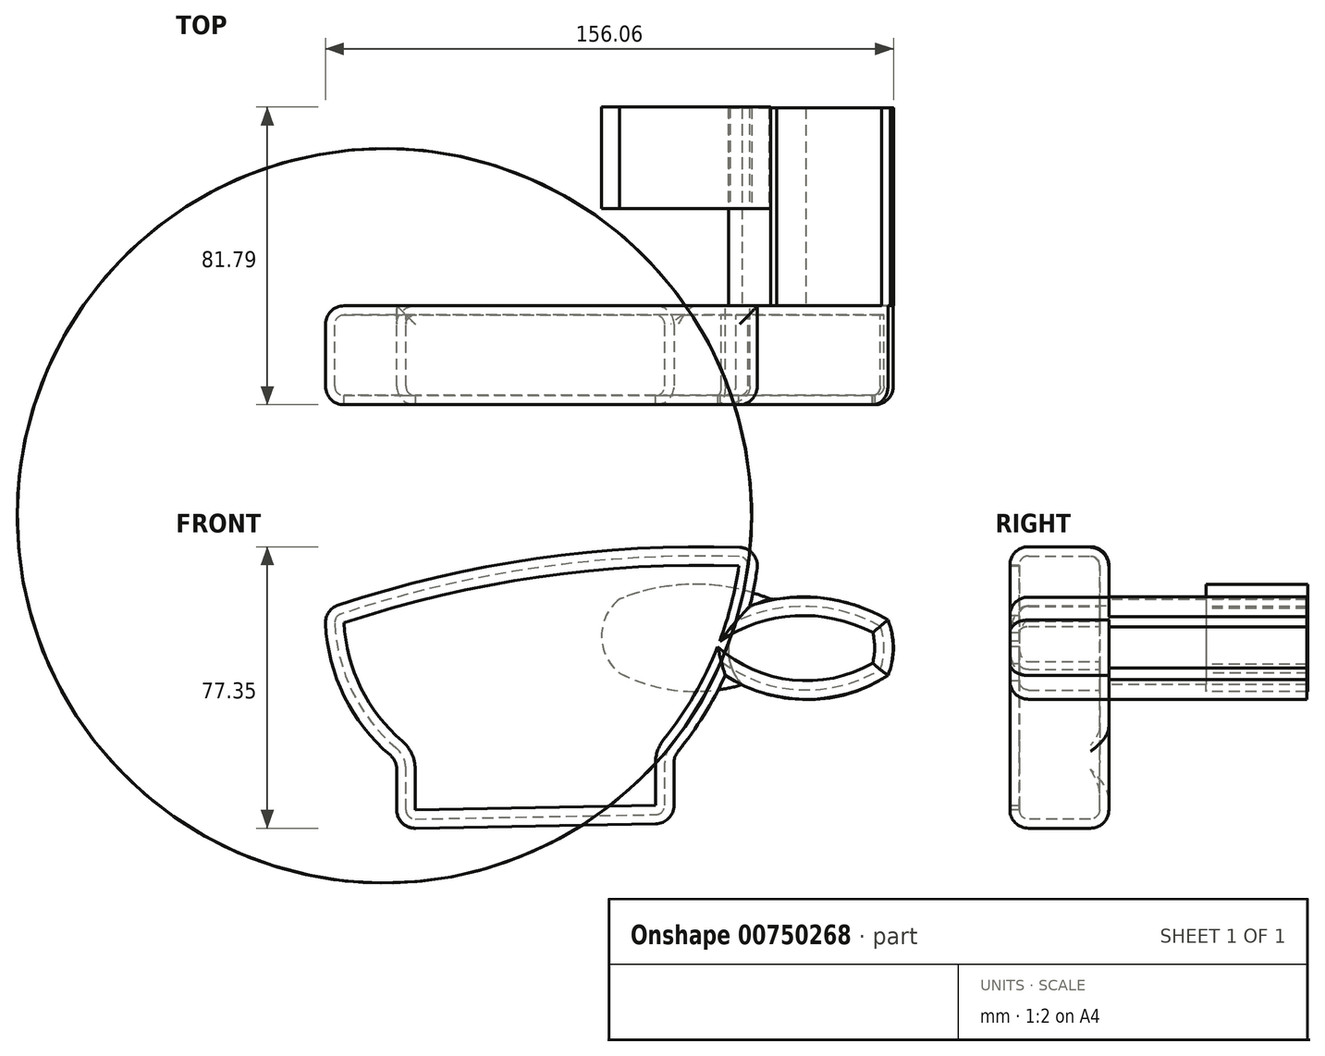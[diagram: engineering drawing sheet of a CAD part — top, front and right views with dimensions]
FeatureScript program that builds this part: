
annotation { "Feature Type Name" : "Feature", "Feature Type Description" : "" }
export const myFeature = defineFeature(function(context is Context, id is Id, definition is map)
    precondition{}
    {
        {
            var Q0;
            Q0=qCreatedBy(makeId("Front.planeOp"),FACE);
            var sketch = newSketch(context, id + "F0", { "sketchPlane" : qUnion([Q0])});
            skLineSegment(sketch, "E0", {"start": v(-61.22, -77.05) * mm, "end": v(-61.22, -58.3) * mm});
            skLineSegment(sketch, "E1", {"start": v(14.97, -75.67) * mm, "end": v(14.97, -57.2) * mm});
            skArc(sketch, "E2", {"start": v(-80.82, -16.86) * mm, "mid": v(-75.96, -39.92) * mm, "end": v(-61.22, -58.3) * mm});
            skLineSegment(sketch, "E3", {"start": v(-61.22, -77.05) * mm, "end": v(14.97, -75.67) * mm});
            skArc(sketch, "E4", {"start": v(38.47, 0) * mm, "mid": v(-21.98, -2.73) * mm, "end": v(-80.82, -16.86) * mm});
            skArc(sketch, "E5", {"start": v(14.97, -57.2) * mm, "mid": v(31.1, -30.4) * mm, "end": v(38.47, 0) * mm});
            skArc(sketch, "E6", {"start": v(73.75, -19.7) * mm, "mid": v(55.22, -13.68) * mm, "end": v(35.85, -15.83) * mm});
            skArc(sketch, "E7", {"start": v(73.75, -35.02) * mm, "mid": v(75.2, -27.36) * mm, "end": v(73.75, -19.7) * mm});
            skArc(sketch, "E8", {"start": v(29.06, -35.02) * mm, "mid": v(51.4, -41.51) * mm, "end": v(73.75, -35.02) * mm});
            skSolve(sketch);
        }
        {
            var Q0;
            Q0=qSketchRegion(id+"F0",true);
            var Q1;
            Q1=makeQuery(id+"F0.imprint","IMPRINT",FACE,{"disambiguationData":[TD([[makeQuery(id+"F0.imprint","IMPRINT",EDGE,{"derivedFrom":sQuery(id+"F0.wireOp",EDGE,"E0")}),-1.0]])]});
            extrude(context, id + "F1", {"entities" : qUnion([Q0, Q1]), "depth" : 27.18 * mm, "offsetDistance" : 25.4 * mm});
        }
        {
            var Q0;
            Q0=makeQuery(id+"F1.opExtrude","SWEPT_FACE",FACE,{"disambiguationData":[OSD([sQuery(id+"F0.wireOp",EDGE,"E2")])]});
            var Q1;
            Q1=makeQuery(id+"F1.opExtrude","SWEPT_FACE",FACE,{"disambiguationData":[OSD([sQuery(id+"F0.wireOp",EDGE,"E4")])]});
            var Q2;
            Q2=makeQuery(id+"F1.opExtrude","CAP_EDGE",EDGE,{"disambiguationData":[OSD([sQuery(id+"F0.wireOp",EDGE,"E3")])],"isStart":false});
            var Q3;
            Q3=makeQuery(id+"F1.opExtrude","SWEPT_FACE",FACE,{"disambiguationData":[OSD([sQuery(id+"F0.wireOp",EDGE,"E3")])]});
            var Q4;
            {var subQ0=sQuery(id+"F0.wireOp",EDGE,"E5");Q4=makeQuery(id+"F1.opExtrude","CAP_EDGE",EDGE,{"disambiguationData":[OSD([subQ0]),TDD([makeQuery(id+"F0.imprint","IMPRINT",EDGE,{"disambiguationData":[TD([[makeQuery(id+"F0.imprint","INTERSECT",VERTEX,{"derivedFrom":[sQuery(id+"F0.wireOp",EDGE,"E1"),subQ0]}),-1.0]])],"derivedFrom":subQ0})])],"isStart":false});}
            var Q5;
            {var subQ0=sQuery(id+"F0.wireOp",EDGE,"E5");Q5=makeQuery(id+"F1.opExtrude","CAP_EDGE",EDGE,{"disambiguationData":[OSD([subQ0]),TDD([makeQuery(id+"F0.imprint","IMPRINT",EDGE,{"disambiguationData":[TD([[makeQuery(id+"F0.imprint","INTERSECT",VERTEX,{"derivedFrom":[sQuery(id+"F0.wireOp",EDGE,"E4"),subQ0]}),1.0]])],"derivedFrom":subQ0})])],"isStart":false});}
            var Q6;
            Q6=makeQuery(id+"F1.opExtrude","SWEPT_FACE",FACE,{"disambiguationData":[OSD([sQuery(id+"F0.wireOp",EDGE,"E1")])]});
            var Q7;
            Q7=makeQuery(id+"F1.opExtrude","CAP_FACE",FACE,{"disambiguationData":[OSD([sQuery(id+"F0.wireOp",EDGE,"E0"),sQuery(id+"F0.wireOp",EDGE,"E1"),sQuery(id+"F0.wireOp",EDGE,"E2"),sQuery(id+"F0.wireOp",EDGE,"E3"),sQuery(id+"F0.wireOp",EDGE,"E4"),sQuery(id+"F0.wireOp",EDGE,"E5"),sQuery(id+"F0.wireOp",EDGE,"E6"),sQuery(id+"F0.wireOp",EDGE,"E7"),sQuery(id+"F0.wireOp",EDGE,"E8")])],"isStart":false});
            fillet(context, id + "F2", {"entities" : qUnion([Q0, Q1, Q2, Q3, Q4, Q5, Q6, Q7]), "radius" : 5.08 * mm, "tangentPropagation" : true, "allowEdgeOverflow" : false});
        }
        {
            var Q0;
            Q0=makeQuery(id+"F1.opExtrude","CAP_FACE",FACE,{"disambiguationData":[OSD([sQuery(id+"F0.wireOp",EDGE,"E0"),sQuery(id+"F0.wireOp",EDGE,"E1"),sQuery(id+"F0.wireOp",EDGE,"E2"),sQuery(id+"F0.wireOp",EDGE,"E3"),sQuery(id+"F0.wireOp",EDGE,"E4"),sQuery(id+"F0.wireOp",EDGE,"E5"),sQuery(id+"F0.wireOp",EDGE,"E6"),sQuery(id+"F0.wireOp",EDGE,"E7"),sQuery(id+"F0.wireOp",EDGE,"E8")])],"isStart":false});
            shell(context, id + "F3", {"entities" : qUnion([Q0]), "thickness" : 2.54 * mm});
        }
        {
            var Q0;
            Q0=qCreatedBy(makeId("Front.planeOp"),FACE);
            var sketch = newSketch(context, id + "F4", { "sketchPlane" : qUnion([Q0])});
            skArc(sketch, "E9", {"start": v(41.5, -14.01) * mm, "mid": v(30.67, -23.43) * mm, "end": v(33.6, -37.49) * mm});
            skArc(sketch, "E10", {"start": v(33.6, -37.49) * mm, "mid": v(42.19, -40.53) * mm, "end": v(51.24, -41.54) * mm});
            skArc(sketch, "E11", {"start": v(51.24, -41.54) * mm, "mid": v(62, -40.29) * mm, "end": v(71.96, -36.07) * mm});
            skArc(sketch, "E12", {"start": v(71.96, -36.07) * mm, "mid": v(73.58, -34.81) * mm, "end": v(74.39, -32.94) * mm});
            skArc(sketch, "E13", {"start": v(74.39, -32.94) * mm, "mid": v(75.28, -27.3) * mm, "end": v(74.39, -21.68) * mm});
            skArc(sketch, "E14", {"start": v(74.39, -21.68) * mm, "mid": v(73.5, -19.95) * mm, "end": v(71.96, -18.78) * mm});
            skArc(sketch, "E15", {"start": v(71.96, -18.78) * mm, "mid": v(65.2, -15.82) * mm, "end": v(58.04, -14.01) * mm});
            skArc(sketch, "E16", {"start": v(58.04, -14.01) * mm, "mid": v(50.61, -13.39) * mm, "end": v(43.18, -14.01) * mm});
            skArc(sketch, "E17", {"start": v(41.5, -14.01) * mm, "mid": v(42.34, -14.08) * mm, "end": v(43.18, -14.01) * mm});
            skSolve(sketch);
        }
        {
            var Q0;
            Q0=qSketchRegion(id+"F4",true);
            extrude(context, id + "F5", {"entities" : qUnion([Q0]), "oppositeDirection" : true, "depth" : 54.36 * mm, "offsetDistance" : 25.4 * mm});
        }
        {
            var Q0;
            Q0=qCreatedBy(makeId("Front.planeOp"),FACE);
            var sketch = newSketch(context, id + "F6", { "sketchPlane" : qUnion([Q0])});
            skArc(sketch, "E18", {"start": v(35.67, -16.53) * mm, "mid": v(30.57, -23.4) * mm, "end": v(30.4, -31.94) * mm});
            skArc(sketch, "E19", {"start": v(30.4, -31.94) * mm, "mid": v(31.73, -34.9) * mm, "end": v(33.61, -37.55) * mm});
            skArc(sketch, "E20", {"start": v(41.53, -14) * mm, "mid": v(38.47, -14.97) * mm, "end": v(35.67, -16.53) * mm});
            skArc(sketch, "E21", {"start": v(0, -34.32) * mm, "mid": v(16.5, -39.16) * mm, "end": v(33.61, -37.55) * mm});
            skArc(sketch, "E22", {"start": v(41.53, -14) * mm, "mid": v(20.77, -9.92) * mm, "end": v(0, -14) * mm});
            skArc(sketch, "E23", {"start": v(0, -14) * mm, "mid": v(-4.9, -24.16) * mm, "end": v(0, -34.32) * mm});
            skSolve(sketch);
        }
        {
            var Q0;
            Q0 = qSketchRegion(id + "F6", true);
            extrude(context, id + "F7", {"entities" : qUnion([Q0]), "operationType" : NewBodyOperationType.ADD, "oppositeDirection" : true, "depth" : 54.6 * mm, "offsetDistance" : 25.4 * mm, "hasSecondDirection" : true, "secondDirectionOppositeDirection" : true, "secondDirectionDepth" : 26.67 * mm});
        }
    });
